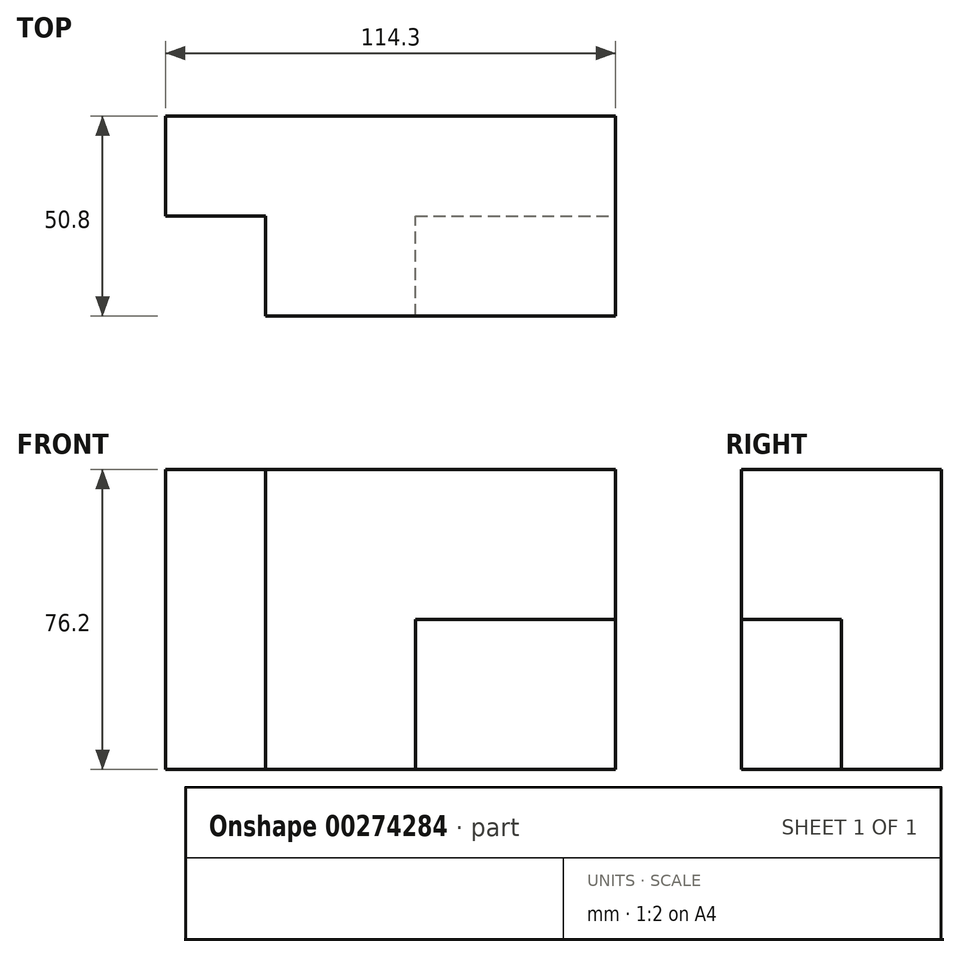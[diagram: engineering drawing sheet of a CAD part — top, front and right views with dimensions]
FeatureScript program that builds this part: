
annotation { "Feature Type Name" : "Feature", "Feature Type Description" : "" }
export const myFeature = defineFeature(function(context is Context, id is Id, definition is map)
    precondition{}
    {
        {
            var Q0;
            Q0=qCreatedBy(makeId("Front.planeOp"),FACE);
            var sketch = newSketch(context, id + "F0", { "sketchPlane" : qUnion([Q0])});
            skLineSegment(sketch, "E0.bottom", {"start": v(0, 0) * mm, "end": v(114.3, 0) * mm});
            skLineSegment(sketch, "E0.top", {"start": v(0, 76.2) * mm, "end": v(114.3, 76.2) * mm});
            skLineSegment(sketch, "E0.left", {"start": v(0, 0) * mm, "end": v(0, 76.2) * mm});
            skLineSegment(sketch, "E0.right", {"start": v(114.3, 0) * mm, "end": v(114.3, 76.2) * mm});
            skSolve(sketch);
        }
        {
            var Q0;
            Q0 = qSketchRegion(id + "F0", true);
            extrude(context, id + "F1", {"entities" : qUnion([Q0]), "depth" : 25.4 * mm});
        }
        {
            var Q0;
            Q0=makeQuery(id+"F1.opExtrude","CAP_FACE",FACE,{"disambiguationData":[OSD([sQuery(id+"F0.wireOp",EDGE,"E0.bottom"),sQuery(id+"F0.wireOp",EDGE,"E0.top"),sQuery(id+"F0.wireOp",EDGE,"E0.left"),sQuery(id+"F0.wireOp",EDGE,"E0.right")])],"isStart":false});
            var sketch = newSketch(context, id + "F2", { "sketchPlane" : qUnion([Q0])});
            skLineSegment(sketch, "E1", {"start": v(114.3, 76.2) * mm, "end": v(25.4, 76.2) * mm});
            skLineSegment(sketch, "E2", {"start": v(25.4, 76.2) * mm, "end": v(25.4, 0) * mm});
            skLineSegment(sketch, "E3", {"start": v(25.4, 0) * mm, "end": v(63.5, 0) * mm});
            skLineSegment(sketch, "E4", {"start": v(63.5, 0) * mm, "end": v(63.5, 38.1) * mm});
            skLineSegment(sketch, "E5", {"start": v(63.5, 38.1) * mm, "end": v(114.3, 38.1) * mm});
            skLineSegment(sketch, "E6", {"start": v(114.3, 38.1) * mm, "end": v(114.3, 76.2) * mm});
            skSolve(sketch);
        }
        {
            var Q0;
            Q0 = qSketchRegion(id + "F2", true);
            extrude(context, id + "F3", {"entities" : qUnion([Q0]), "operationType" : NewBodyOperationType.ADD, "depth" : 25.4 * mm});
        }
    });
